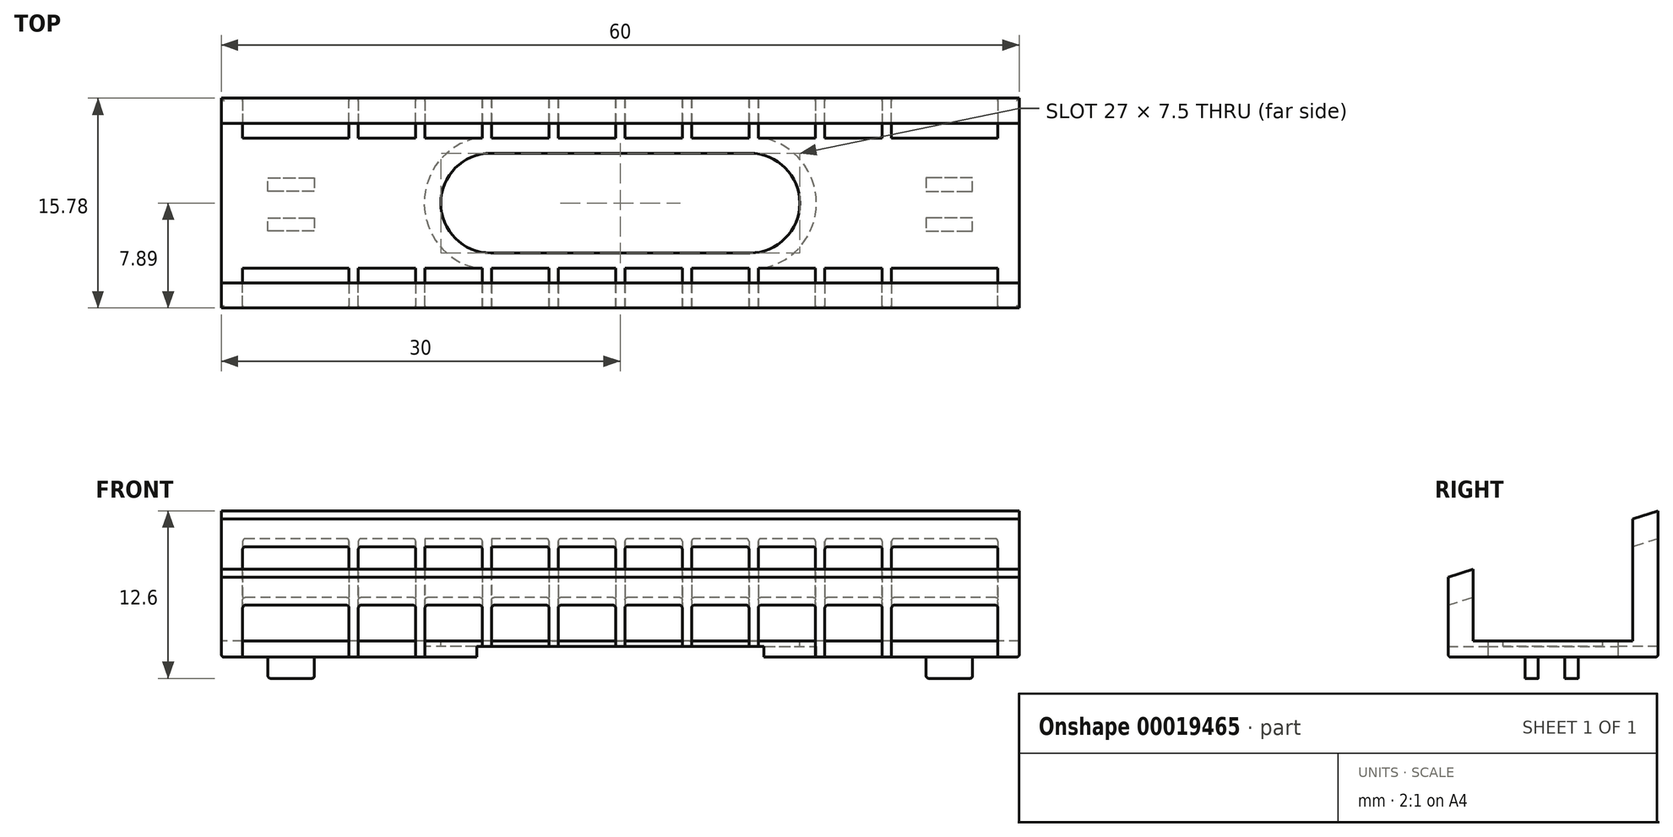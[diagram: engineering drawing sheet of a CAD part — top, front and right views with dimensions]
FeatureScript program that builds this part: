
annotation { "Feature Type Name" : "Feature", "Feature Type Description" : "" }
export const myFeature = defineFeature(function(context is Context, id is Id, definition is map)
    precondition{}
    {
        {
            var Q0;
            Q0=qCreatedBy(makeId("Top.planeOp"),FACE);
            var sketch = newSketch(context, id + "F0", { "sketchPlane" : qUnion([Q0])});
            skLineSegment(sketch, "E0.bottom", {"start": v(0, 0) * mm, "end": v(-60, 0) * mm});
            skLineSegment(sketch, "E0.top", {"start": v(0, 15.78) * mm, "end": v(-60, 15.78) * mm});
            skLineSegment(sketch, "E0.left", {"start": v(0, 0) * mm, "end": v(0, 15.78) * mm});
            skLineSegment(sketch, "E0.right", {"start": v(-60, 0) * mm, "end": v(-60, 15.78) * mm});
            skSolve(sketch);
        }
        {
            var Q0;
            Q0 = qSketchRegion(id + "F0", true);
            extrude(context, id + "F1", {"entities" : qUnion([Q0]), "depth" : 11 * mm});
        }
        {
            var Q0;
            Q0=makeQuery(id+"F1.opExtrude","SWEPT_FACE",FACE,{"disambiguationData":[OSD([sQuery(id+"F0.wireOp",EDGE,"E0.right")])]});
            var sketch = newSketch(context, id + "F2", { "sketchPlane" : qUnion([Q0])});
            skLineSegment(sketch, "E1", {"start": v(0, 6) * mm, "end": v(-1.89, 6.6) * mm});
            skLineSegment(sketch, "E2", {"start": v(-1.89, 6.6) * mm, "end": v(-1.89, 1.2) * mm});
            skLineSegment(sketch, "E3", {"start": v(-1.89, 1.2) * mm, "end": v(-13.89, 1.2) * mm});
            skLineSegment(sketch, "E4", {"start": v(-13.89, 1.2) * mm, "end": v(-13.89, 10.4) * mm});
            skLineSegment(sketch, "E5.trimOffspring", {"start": v(-13.89, 10.4) * mm, "end": v(-15.78, 11) * mm});
            skLineSegment(sketch, "E6", {"start": v(-7.89, 0) * mm, "end": v(-7.89, 1.2) * mm, "construction": true});
            skSolve(sketch);
        }
        {
            var Q0;
            {var subQ2=sQuery(id+"F2.wireOp",EDGE,"E1");Q0=makeQuery(id+"F2.imprint","IMPRINT",FACE,{"disambiguationData":[TD([[makeQuery(id+"F2.imprint","IMPRINT",EDGE,{"derivedFrom":subQ2}),-1.0]])]});}
            extrude(context, id + "F3", {"entities" : qUnion([Q0]), "operationType" : NewBodyOperationType.REMOVE, "endBound" : BoundingType.THROUGH_ALL, "oppositeDirection" : true, "depth" : 25 * mm});
        }
        {
            var Q0;
            Q0=makeQuery(id+"F3.boolean.opBoolean","COPY",FACE,{"derivedFrom":makeQuery(id+"F3.opExtrude","SWEPT_FACE",FACE,{"disambiguationData":[OSD([sQuery(id+"F2.wireOp",EDGE,"E3")])]})});
            var sketch = newSketch(context, id + "F4", { "sketchPlane" : qUnion([Q0])});
            skLineSegment(sketch, "E7", {"start": v(-30, 11.64) * mm, "end": v(-22.65, 11.64) * mm});
            skLineSegment(sketch, "E8", {"start": v(-30, 4.14) * mm, "end": v(-22.65, 4.14) * mm});
            skPoint(sketch, "E9.orphan", {"position": v(-41.1, 11.64) * mm});
            skPoint(sketch, "E10.orphan", {"position": v(-41.1, 4.14) * mm});
            skPoint(sketch, "E11.start.orphan", {"position": v(-18.9, 11.64) * mm});
            skPoint(sketch, "E12.orphan", {"position": v(-18.9, 4.14) * mm});
            skLineSegment(sketch, "E13", {"start": v(-60, 7.89) * mm, "end": v(0, 7.89) * mm, "construction": true});
            skLineSegment(sketch, "E14", {"start": v(-30, 13.89) * mm, "end": v(-30, 1.89) * mm, "construction": true});
            skLineSegment(sketch, "E15", {"start": v(-30, 7.89) * mm, "end": v(-20.25, 7.89) * mm, "construction": true});
            skArc(sketch, "E16", {"start": v(-20.25, 4.14) * mm, "mid": v(-16.5, 7.89) * mm, "end": v(-20.25, 11.64) * mm});
            skLineSegment(sketch, "E17", {"start": v(-22.65, 11.64) * mm, "end": v(-20.25, 11.64) * mm});
            skLineSegment(sketch, "E18", {"start": v(-22.65, 4.14) * mm, "end": v(-20.25, 4.14) * mm});
            skLineSegment(sketch, "E19.MirrorCS", {"start": v(-30, 4.14) * mm, "end": v(-37.35, 4.14) * mm});
            skLineSegment(sketch, "E20.MirrorCS", {"start": v(-37.35, 4.14) * mm, "end": v(-39.75, 4.14) * mm});
            skArc(sketch, "E21.MirrorCS", {"start": v(-39.75, 4.14) * mm, "mid": v(-43.5, 7.89) * mm, "end": v(-39.75, 11.64) * mm});
            skLineSegment(sketch, "E22.MirrorCS", {"start": v(-37.35, 11.64) * mm, "end": v(-39.75, 11.64) * mm});
            skLineSegment(sketch, "E23.MirrorCS", {"start": v(-30, 11.64) * mm, "end": v(-37.35, 11.64) * mm});
            skSolve(sketch);
        }
        {
            var Q0;
            Q0 = qSketchRegion(id + "F4", true);
            extrude(context, id + "F5", {"entities" : qUnion([Q0]), "operationType" : NewBodyOperationType.REMOVE, "endBound" : BoundingType.THROUGH_ALL, "oppositeDirection" : true, "depth" : 25 * mm});
        }
        {
            var Q0;
            Q0=makeQuery(id+"F1.opExtrude","CAP_FACE",FACE,{"disambiguationData":[OSD([sQuery(id+"F0.wireOp",EDGE,"E0.bottom"),sQuery(id+"F0.wireOp",EDGE,"E0.top"),sQuery(id+"F0.wireOp",EDGE,"E0.left"),sQuery(id+"F0.wireOp",EDGE,"E0.right")])],"isStart":true});
            var sketch = newSketch(context, id + "F6", { "sketchPlane" : qUnion([Q0])});
            skLineSegment(sketch, "E24", {"start": v(0, 0) * mm, "end": v(-1.6, 0) * mm});
            skLineSegment(sketch, "E25", {"start": v(-1.6, 0) * mm, "end": v(-1.6, -3) * mm});
            skLineSegment(sketch, "E26", {"start": v(-1.6, -3) * mm, "end": v(-9.6, -3) * mm});
            skLineSegment(sketch, "E27", {"start": v(-9.6, -3) * mm, "end": v(-9.6, 0) * mm});
            skLineSegment(sketch, "E28", {"start": v(-9.6, 0) * mm, "end": v(-10.3, 0) * mm});
            skLineSegment(sketch, "E29", {"start": v(-10.3, 0) * mm, "end": v(-10.3, -3) * mm});
            skLineSegment(sketch, "E30", {"start": v(-10.3, -3) * mm, "end": v(-14.61, -3) * mm});
            skLineSegment(sketch, "E31", {"start": v(-14.61, -3) * mm, "end": v(-14.61, 0) * mm});
            skLineSegment(sketch, "E32", {"start": v(-14.61, 0) * mm, "end": v(-15.31, 0) * mm});
            skLineSegment(sketch, "E33", {"start": v(-15.31, 0) * mm, "end": v(-15.31, -3) * mm});
            skLineSegment(sketch, "E34", {"start": v(-15.31, -3) * mm, "end": v(-19.62, -3) * mm});
            skLineSegment(sketch, "E35", {"start": v(-19.63, -3) * mm, "end": v(-19.63, 0) * mm});
            skLineSegment(sketch, "E36", {"start": v(-19.63, 0) * mm, "end": v(-20.33, 0) * mm});
            skLineSegment(sketch, "E37", {"start": v(-20.33, 0) * mm, "end": v(-20.33, -3) * mm});
            skLineSegment(sketch, "E38", {"start": v(-20.32, -3) * mm, "end": v(-24.64, -3) * mm});
            skLineSegment(sketch, "E39", {"start": v(-24.64, -3) * mm, "end": v(-24.64, 0) * mm});
            skLineSegment(sketch, "E40", {"start": v(-24.64, 0) * mm, "end": v(-25.34, 0) * mm});
            skLineSegment(sketch, "E41", {"start": v(-25.34, 0) * mm, "end": v(-25.34, -3) * mm});
            skLineSegment(sketch, "E42", {"start": v(-25.34, -3) * mm, "end": v(-29.65, -3) * mm});
            skLineSegment(sketch, "E43", {"start": v(-29.65, -3) * mm, "end": v(-29.65, 0) * mm});
            skLineSegment(sketch, "E44", {"start": v(-29.65, 0) * mm, "end": v(-30, 0) * mm});
            skLineSegment(sketch, "E45.MirrorCS", {"start": v(-30.35, -3) * mm, "end": v(-30.35, 0) * mm});
            skLineSegment(sketch, "E46.MirrorCS", {"start": v(-34.66, -3) * mm, "end": v(-30.35, -3) * mm});
            skLineSegment(sketch, "E47.MirrorCS", {"start": v(-34.66, 0) * mm, "end": v(-34.66, -3) * mm});
            skLineSegment(sketch, "E48.MirrorCS", {"start": v(-35.36, -3) * mm, "end": v(-35.36, 0) * mm});
            skLineSegment(sketch, "E49.MirrorCS", {"start": v(-39.68, -3) * mm, "end": v(-35.36, -3) * mm});
            skLineSegment(sketch, "E50.MirrorCS", {"start": v(-39.67, 0) * mm, "end": v(-39.67, -3) * mm});
            skLineSegment(sketch, "E51.MirrorCS", {"start": v(-40.37, -3) * mm, "end": v(-40.37, 0) * mm});
            skLineSegment(sketch, "E52.MirrorCS", {"start": v(-44.69, -3) * mm, "end": v(-40.38, -3) * mm});
            skLineSegment(sketch, "E53.MirrorCS", {"start": v(-44.69, 0) * mm, "end": v(-44.69, -3) * mm});
            skLineSegment(sketch, "E54.MirrorCS", {"start": v(-45.39, -3) * mm, "end": v(-45.39, 0) * mm});
            skLineSegment(sketch, "E55.MirrorCS", {"start": v(-49.7, -3) * mm, "end": v(-45.39, -3) * mm});
            skLineSegment(sketch, "E56.MirrorCS", {"start": v(-49.7, 0) * mm, "end": v(-49.7, -3) * mm});
            skLineSegment(sketch, "E57.MirrorCS", {"start": v(-50.4, -3) * mm, "end": v(-50.4, 0) * mm});
            skLineSegment(sketch, "E58.MirrorCS", {"start": v(-58.4, -3) * mm, "end": v(-50.4, -3) * mm});
            skLineSegment(sketch, "E59.MirrorCS", {"start": v(-58.4, 0) * mm, "end": v(-58.4, -3) * mm});
            skLineSegment(sketch, "E60.MirrorCS", {"start": v(-58.4, -15.78) * mm, "end": v(-58.4, -12.78) * mm});
            skLineSegment(sketch, "E61.MirrorCS", {"start": v(-58.4, -12.78) * mm, "end": v(-50.4, -12.78) * mm});
            skLineSegment(sketch, "E62.MirrorCS", {"start": v(-50.4, -12.78) * mm, "end": v(-50.4, -15.78) * mm});
            skLineSegment(sketch, "E63.MirrorCS", {"start": v(-49.7, -15.78) * mm, "end": v(-49.7, -12.78) * mm});
            skLineSegment(sketch, "E64.MirrorCS", {"start": v(-49.7, -12.78) * mm, "end": v(-45.39, -12.78) * mm});
            skLineSegment(sketch, "E65.MirrorCS", {"start": v(-45.39, -12.78) * mm, "end": v(-45.39, -15.78) * mm});
            skLineSegment(sketch, "E66.MirrorCS", {"start": v(-44.69, -15.78) * mm, "end": v(-44.69, -12.78) * mm});
            skLineSegment(sketch, "E67.MirrorCS", {"start": v(-44.69, -12.78) * mm, "end": v(-40.38, -12.78) * mm});
            skLineSegment(sketch, "E68.MirrorCS", {"start": v(-40.37, -12.78) * mm, "end": v(-40.37, -15.78) * mm});
            skLineSegment(sketch, "E69.MirrorCS", {"start": v(-39.67, -15.78) * mm, "end": v(-39.67, -12.78) * mm});
            skLineSegment(sketch, "E70.MirrorCS", {"start": v(-39.68, -12.78) * mm, "end": v(-35.36, -12.78) * mm});
            skLineSegment(sketch, "E71.MirrorCS", {"start": v(-35.36, -12.78) * mm, "end": v(-35.36, -15.78) * mm});
            skLineSegment(sketch, "E72.MirrorCS", {"start": v(-34.66, -12.78) * mm, "end": v(-30.35, -12.78) * mm});
            skLineSegment(sketch, "E73.MirrorCS", {"start": v(-30.35, -12.78) * mm, "end": v(-30.35, -15.78) * mm});
            skLineSegment(sketch, "E74.MirrorCS", {"start": v(-29.65, -12.78) * mm, "end": v(-29.65, -15.78) * mm});
            skLineSegment(sketch, "E75.MirrorCS", {"start": v(-25.34, -12.78) * mm, "end": v(-29.65, -12.78) * mm});
            skLineSegment(sketch, "E76.MirrorCS", {"start": v(-25.34, -15.78) * mm, "end": v(-25.34, -12.78) * mm});
            skLineSegment(sketch, "E77.MirrorCS", {"start": v(-24.64, -12.78) * mm, "end": v(-24.64, -15.78) * mm});
            skLineSegment(sketch, "E78.MirrorCS", {"start": v(-20.32, -12.78) * mm, "end": v(-24.64, -12.78) * mm});
            skLineSegment(sketch, "E79.MirrorCS", {"start": v(-20.33, -15.78) * mm, "end": v(-20.33, -12.78) * mm});
            skLineSegment(sketch, "E80.MirrorCS", {"start": v(-15.31, -12.78) * mm, "end": v(-19.62, -12.78) * mm});
            skLineSegment(sketch, "E81.MirrorCS", {"start": v(-15.31, -15.78) * mm, "end": v(-15.31, -12.78) * mm});
            skLineSegment(sketch, "E82.MirrorCS", {"start": v(-14.61, -12.78) * mm, "end": v(-14.61, -15.78) * mm});
            skLineSegment(sketch, "E83.MirrorCS", {"start": v(-10.3, -12.78) * mm, "end": v(-14.61, -12.78) * mm});
            skLineSegment(sketch, "E84.MirrorCS", {"start": v(-10.3, -15.78) * mm, "end": v(-10.3, -12.78) * mm});
            skLineSegment(sketch, "E85.MirrorCS", {"start": v(-9.6, -12.78) * mm, "end": v(-9.6, -15.78) * mm});
            skLineSegment(sketch, "E86.MirrorCS", {"start": v(-1.6, -12.78) * mm, "end": v(-9.6, -12.78) * mm});
            skLineSegment(sketch, "E87.MirrorCS", {"start": v(-1.6, -15.78) * mm, "end": v(-1.6, -12.78) * mm});
            skLineSegment(sketch, "E88", {"start": v(-19.62, -12.78) * mm, "end": v(-19.62, -15.78) * mm});
            skLineSegment(sketch, "E89", {"start": v(-34.66, -12.78) * mm, "end": v(-34.66, -15.78) * mm});
            skSolve(sketch);
        }
        {
            var Q0;
            Q0=makeQuery(id+"F3.boolean.opBoolean","COPY",FACE,{"derivedFrom":makeQuery(id+"F3.opExtrude","SWEPT_FACE",FACE,{"disambiguationData":[OSD([sQuery(id+"F2.wireOp",EDGE,"E5.trimOffspring")])]})});
            cPlane(context, id + "F7", {"entities" : qUnion([Q0]), "cplaneType" : CPlaneType.OFFSET, "offset" : 2 * mm, "oppositeDirection" : true, "width" : 150 * mm, "height" : 150 * mm});
        }
        {
            var Q0;
            Q0 = qSketchRegion(id + "F6", true);
            var Q1;
            {var subQ2=sQuery(id+"F6.wireOp",EDGE,"E60.MirrorCS");Q1=makeQuery(id+"F6.imprint","IMPRINT",FACE,{"disambiguationData":[TD([[makeQuery(id+"F6.imprint","IMPRINT",EDGE,{"derivedFrom":subQ2}),-1.0]])]});}
            var Q2;
            {var subQ2=sQuery(id+"F6.wireOp",EDGE,"E63.MirrorCS");Q2=makeQuery(id+"F6.imprint","IMPRINT",FACE,{"disambiguationData":[TD([[makeQuery(id+"F6.imprint","IMPRINT",EDGE,{"derivedFrom":subQ2}),-1.0]])]});}
            var Q3;
            {var subQ2=sQuery(id+"F6.wireOp",EDGE,"E66.MirrorCS");Q3=makeQuery(id+"F6.imprint","IMPRINT",FACE,{"disambiguationData":[TD([[makeQuery(id+"F6.imprint","IMPRINT",EDGE,{"derivedFrom":subQ2}),-1.0]])]});}
            var Q4;
            {var subQ2=sQuery(id+"F6.wireOp",EDGE,"E69.MirrorCS");Q4=makeQuery(id+"F6.imprint","IMPRINT",FACE,{"disambiguationData":[TD([[makeQuery(id+"F6.imprint","IMPRINT",EDGE,{"derivedFrom":subQ2}),-1.0]])]});}
            var Q5;
            Q5=makeQuery(id+"F6.imprint","IMPRINT",FACE,{"disambiguationData":[TD([[makeQuery(id+"F6.imprint","IMPRINT",EDGE,{"derivedFrom":sQuery(id+"F6.wireOp",EDGE,"E72.MirrorCS")}),-1.0]])]});
            var Q6;
            {var subQ2=sQuery(id+"F6.wireOp",EDGE,"E74.MirrorCS");Q6=makeQuery(id+"F6.imprint","IMPRINT",FACE,{"disambiguationData":[TD([[makeQuery(id+"F6.imprint","IMPRINT",EDGE,{"derivedFrom":subQ2}),1.0]])]});}
            var Q7;
            {var subQ2=sQuery(id+"F6.wireOp",EDGE,"E77.MirrorCS");Q7=makeQuery(id+"F6.imprint","IMPRINT",FACE,{"disambiguationData":[TD([[makeQuery(id+"F6.imprint","IMPRINT",EDGE,{"derivedFrom":subQ2}),1.0]])]});}
            var Q8;
            Q8=makeQuery(id+"F6.imprint","IMPRINT",FACE,{"disambiguationData":[TD([[makeQuery(id+"F6.imprint","IMPRINT",EDGE,{"derivedFrom":sQuery(id+"F6.wireOp",EDGE,"E80.MirrorCS")}),1.0]])]});
            var Q9;
            {var subQ2=sQuery(id+"F6.wireOp",EDGE,"E82.MirrorCS");Q9=makeQuery(id+"F6.imprint","IMPRINT",FACE,{"disambiguationData":[TD([[makeQuery(id+"F6.imprint","IMPRINT",EDGE,{"derivedFrom":subQ2}),1.0]])]});}
            var Q10;
            {var subQ2=sQuery(id+"F6.wireOp",EDGE,"E85.MirrorCS");Q10=makeQuery(id+"F6.imprint","IMPRINT",FACE,{"disambiguationData":[TD([[makeQuery(id+"F6.imprint","IMPRINT",EDGE,{"derivedFrom":subQ2}),1.0]])]});}
            var Q11;
            {var subQ2=sQuery(id+"F6.wireOp",EDGE,"E57.MirrorCS");Q11=makeQuery(id+"F6.imprint","IMPRINT",FACE,{"disambiguationData":[TD([[makeQuery(id+"F6.imprint","IMPRINT",EDGE,{"derivedFrom":subQ2}),1.0]])]});}
            var Q12;
            {var subQ2=sQuery(id+"F6.wireOp",EDGE,"E54.MirrorCS");Q12=makeQuery(id+"F6.imprint","IMPRINT",FACE,{"disambiguationData":[TD([[makeQuery(id+"F6.imprint","IMPRINT",EDGE,{"derivedFrom":subQ2}),1.0]])]});}
            var Q13;
            {var subQ2=sQuery(id+"F6.wireOp",EDGE,"E51.MirrorCS");Q13=makeQuery(id+"F6.imprint","IMPRINT",FACE,{"disambiguationData":[TD([[makeQuery(id+"F6.imprint","IMPRINT",EDGE,{"derivedFrom":subQ2}),1.0]])]});}
            var Q14;
            {var subQ2=sQuery(id+"F6.wireOp",EDGE,"E48.MirrorCS");Q14=makeQuery(id+"F6.imprint","IMPRINT",FACE,{"disambiguationData":[TD([[makeQuery(id+"F6.imprint","IMPRINT",EDGE,{"derivedFrom":subQ2}),1.0]])]});}
            var Q15;
            {var subQ2=sQuery(id+"F6.wireOp",EDGE,"E45.MirrorCS");Q15=makeQuery(id+"F6.imprint","IMPRINT",FACE,{"disambiguationData":[TD([[makeQuery(id+"F6.imprint","IMPRINT",EDGE,{"derivedFrom":subQ2}),1.0]])]});}
            var Q16;
            {var subQ2=sQuery(id+"F6.wireOp",EDGE,"E41");Q16=makeQuery(id+"F6.imprint","IMPRINT",FACE,{"disambiguationData":[TD([[makeQuery(id+"F6.imprint","IMPRINT",EDGE,{"derivedFrom":subQ2}),-1.0]])]});}
            var Q17;
            {var subQ2=sQuery(id+"F6.wireOp",EDGE,"E37");Q17=makeQuery(id+"F6.imprint","IMPRINT",FACE,{"disambiguationData":[TD([[makeQuery(id+"F6.imprint","IMPRINT",EDGE,{"derivedFrom":subQ2}),-1.0]])]});}
            var Q18;
            {var subQ2=sQuery(id+"F6.wireOp",EDGE,"E33");Q18=makeQuery(id+"F6.imprint","IMPRINT",FACE,{"disambiguationData":[TD([[makeQuery(id+"F6.imprint","IMPRINT",EDGE,{"derivedFrom":subQ2}),-1.0]])]});}
            var Q19;
            {var subQ2=sQuery(id+"F6.wireOp",EDGE,"E29");Q19=makeQuery(id+"F6.imprint","IMPRINT",FACE,{"disambiguationData":[TD([[makeQuery(id+"F6.imprint","IMPRINT",EDGE,{"derivedFrom":subQ2}),-1.0]])]});}
            var Q20;
            {var subQ2=sQuery(id+"F6.wireOp",EDGE,"E25");Q20=makeQuery(id+"F6.imprint","IMPRINT",FACE,{"disambiguationData":[TD([[makeQuery(id+"F6.imprint","IMPRINT",EDGE,{"derivedFrom":subQ2}),-1.0]])]});}
            var Q21;
            Q21=qCreatedBy(id+"F7.planeOp",FACE);
            extrude(context, id + "F8", {"entities" : qUnion([Q0, Q1, Q2, Q3, Q4, Q5, Q6, Q7, Q8, Q9, Q10, Q11, Q12, Q13, Q14, Q15, Q16, Q17, Q18, Q19, Q20]), "operationType" : NewBodyOperationType.REMOVE, "endBound" : BoundingType.UP_TO_SURFACE, "oppositeDirection" : true, "endBoundEntityFace" : qUnion([Q21]), "depth" : 25 * mm});
        }
        {
            var Q0;
            Q0=makeQuery(id+"F1.opExtrude","CAP_FACE",FACE,{"disambiguationData":[OSD([sQuery(id+"F0.wireOp",EDGE,"E0.bottom"),sQuery(id+"F0.wireOp",EDGE,"E0.top"),sQuery(id+"F0.wireOp",EDGE,"E0.left"),sQuery(id+"F0.wireOp",EDGE,"E0.right")])],"isStart":true});
            var sketch = newSketch(context, id + "F9", { "sketchPlane" : qUnion([Q0])});
            skArc(sketch, "E90", {"start": v(-19.2, -12.78) * mm, "mid": v(-15.25, -7.9) * mm, "end": v(-19.2, -3) * mm});
            skArc(sketch, "E91", {"start": v(-40.8, -3) * mm, "mid": v(-44.75, -7.9) * mm, "end": v(-40.8, -12.78) * mm});
            skLineSegment(sketch, "E92", {"start": v(-19.2, -12.78) * mm, "end": v(-19.2, -15.78) * mm});
            skLineSegment(sketch, "E93", {"start": v(-19.2, -3) * mm, "end": v(-19.2, 0) * mm});
            skLineSegment(sketch, "E94", {"start": v(-40.8, -12.78) * mm, "end": v(-40.8, -15.78) * mm});
            skLineSegment(sketch, "E95", {"start": v(-40.8, -3) * mm, "end": v(-40.8, 0) * mm});
            skLineSegment(sketch, "E96", {"start": v(-19.2, -15.78) * mm, "end": v(-40.8, -15.78) * mm});
            skLineSegment(sketch, "E97", {"start": v(-40.8, 0) * mm, "end": v(-19.2, 0) * mm});
            skSolve(sketch);
        }
        {
            var Q0;
            Q0 = qSketchRegion(id + "F9", true);
            var Q1;
            {var subQ5=sQuery(id+"F9.wireOp",EDGE,"97906bd3-8b50-4044-a8e2-cee471d0c885");Q1=makeQuery(id+"F9.imprint","IMPRINT",FACE,{"disambiguationData":[TD([[makeQuery(id+"F9.imprint","IMPRINT",EDGE,{"derivedFrom":subQ5}),1.0]])]});}
            extrude(context, id + "F10", {"entities" : qUnion([Q0, Q1]), "operationType" : NewBodyOperationType.REMOVE, "oppositeDirection" : true, "depth" : 0.8 * mm});
        }
        {
            var Q0;
            {var subQ0=sQuery(id+"F0.wireOp",EDGE,"E0.bottom");var subQ1=sQuery(id+"F0.wireOp",EDGE,"E0.top");var subQ2=sQuery(id+"F0.wireOp",EDGE,"E0.left");Q0=makeQuery(id+"F10.boolean.opBoolean","SPLIT",FACE,{"disambiguationData":[TD([makeQuery(id+"F1.opExtrude","SWEPT_FACE",FACE,{"disambiguationData":[OSD([subQ2])]})])],"derivedFrom":makeQuery(id+"F1.opExtrude","CAP_FACE",FACE,{"disambiguationData":[OSD([subQ0,subQ1,subQ2,sQuery(id+"F0.wireOp",EDGE,"E0.right")])],"isStart":true})});}
            var sketch = newSketch(context, id + "F11", { "sketchPlane" : qUnion([Q0])});
            skLineSegment(sketch, "E98", {"start": v(-7, -5.78) * mm, "end": v(-3.5, -5.78) * mm});
            skLineSegment(sketch, "E99", {"start": v(-3.5, -5.78) * mm, "end": v(-3.5, -6.78) * mm});
            skLineSegment(sketch, "E100", {"start": v(-3.5, -6.78) * mm, "end": v(-7, -6.78) * mm});
            skLineSegment(sketch, "E101", {"start": v(-7, -6.78) * mm, "end": v(-7, -5.78) * mm});
            skLineSegment(sketch, "E102", {"start": v(-7, -8.78) * mm, "end": v(-3.5, -8.78) * mm});
            skLineSegment(sketch, "E103", {"start": v(-3.5, -8.78) * mm, "end": v(-3.5, -9.78) * mm});
            skLineSegment(sketch, "E104", {"start": v(-3.5, -9.78) * mm, "end": v(-7, -9.78) * mm});
            skLineSegment(sketch, "E105", {"start": v(-7, -9.78) * mm, "end": v(-7, -8.78) * mm});
            skLineSegment(sketch, "E106.MirrorCS", {"start": v(-53, -6.78) * mm, "end": v(-53, -5.78) * mm});
            skLineSegment(sketch, "E107.MirrorCS", {"start": v(-53, -5.78) * mm, "end": v(-56.5, -5.78) * mm});
            skLineSegment(sketch, "E108.MirrorCS", {"start": v(-56.5, -5.78) * mm, "end": v(-56.5, -6.78) * mm});
            skLineSegment(sketch, "E109.MirrorCS", {"start": v(-56.5, -6.78) * mm, "end": v(-53, -6.78) * mm});
            skLineSegment(sketch, "E110.MirrorCS", {"start": v(-53, -8.78) * mm, "end": v(-56.5, -8.78) * mm});
            skLineSegment(sketch, "E111.MirrorCS", {"start": v(-56.5, -9.78) * mm, "end": v(-53, -9.78) * mm});
            skLineSegment(sketch, "E112.MirrorCS", {"start": v(-53, -9.78) * mm, "end": v(-53, -8.78) * mm});
            skLineSegment(sketch, "E113.MirrorCS", {"start": v(-56.5, -8.78) * mm, "end": v(-56.5, -9.78) * mm});
            skSolve(sketch);
        }
        {
            var Q0;
            Q0 = qSketchRegion(id + "F11", true);
            extrude(context, id + "F12", {"entities" : qUnion([Q0]), "operationType" : NewBodyOperationType.ADD, "depth" : 1.6 * mm});
        }
        {
            var Q0;
            {var subQ0=sQuery(id+"F0.wireOp",EDGE,"E0.bottom");var subQ1=sQuery(id+"F0.wireOp",EDGE,"E0.right");Q0=makeQuery(id+"F8.boolean.opBoolean","SPLIT",EDGE,{"disambiguationData":[TD([makeQuery(id+"F1.opExtrude","SWEPT_FACE",FACE,{"disambiguationData":[OSD([subQ1])]})])],"derivedFrom":makeQuery(id+"F1.opExtrude","CAP_EDGE",EDGE,{"disambiguationData":[OSD([subQ0])],"isStart":true})});}
            var Q1;
            {var subQ0=sQuery(id+"F0.wireOp",EDGE,"E0.right");var subQ1=sQuery(id+"F0.wireOp",EDGE,"E0.top");Q1=makeQuery(id+"F8.boolean.opBoolean","SPLIT",EDGE,{"disambiguationData":[TD([makeQuery(id+"F1.opExtrude","SWEPT_FACE",FACE,{"disambiguationData":[OSD([subQ0])]})])],"derivedFrom":makeQuery(id+"F1.opExtrude","CAP_EDGE",EDGE,{"disambiguationData":[OSD([subQ1])],"isStart":true})});}
            var Q2;
            {var subQ0=sQuery(id+"F0.wireOp",EDGE,"E0.left");var subQ1=sQuery(id+"F0.wireOp",EDGE,"E0.top");Q2=makeQuery(id+"F8.boolean.opBoolean","SPLIT",EDGE,{"disambiguationData":[TD([makeQuery(id+"F1.opExtrude","SWEPT_FACE",FACE,{"disambiguationData":[OSD([subQ0])]})])],"derivedFrom":makeQuery(id+"F1.opExtrude","CAP_EDGE",EDGE,{"disambiguationData":[OSD([subQ1])],"isStart":true})});}
            var Q3;
            {var subQ0=sQuery(id+"F0.wireOp",EDGE,"E0.bottom");var subQ1=sQuery(id+"F0.wireOp",EDGE,"E0.left");Q3=makeQuery(id+"F8.boolean.opBoolean","SPLIT",EDGE,{"disambiguationData":[TD([makeQuery(id+"F1.opExtrude","SWEPT_FACE",FACE,{"disambiguationData":[OSD([subQ1])]})])],"derivedFrom":makeQuery(id+"F1.opExtrude","CAP_EDGE",EDGE,{"disambiguationData":[OSD([subQ0])],"isStart":true})});}
            var Q4;
            Q4=makeQuery(id+"F1.opExtrude","CAP_EDGE",EDGE,{"disambiguationData":[OSD([sQuery(id+"F0.wireOp",EDGE,"E0.left")])],"isStart":true});
            var Q5;
            Q5=makeQuery(id+"F1.opExtrude","CAP_EDGE",EDGE,{"disambiguationData":[OSD([sQuery(id+"F0.wireOp",EDGE,"E0.right")])],"isStart":true});
            var Q6;
            Q6=makeQuery(id+"F8.boolean.opBoolean","COPY",EDGE,{"derivedFrom":makeQuery(id+"F8.opExtrude","CAP_EDGE",EDGE,{"disambiguationData":[OSD([sQuery(id+"F6.wireOp",EDGE,"E60.MirrorCS")])],"isStart":false})});
            var Q7;
            Q7=makeQuery(id+"F8.boolean.opBoolean","COPY",EDGE,{"derivedFrom":makeQuery(id+"F8.opExtrude","CAP_EDGE",EDGE,{"disambiguationData":[OSD([sQuery(id+"F6.wireOp",EDGE,"E63.MirrorCS")])],"isStart":false})});
            var Q8;
            Q8=makeQuery(id+"F8.boolean.opBoolean","COPY",EDGE,{"derivedFrom":makeQuery(id+"F8.opExtrude","CAP_EDGE",EDGE,{"disambiguationData":[OSD([sQuery(id+"F6.wireOp",EDGE,"E62.MirrorCS")])],"isStart":false})});
            var Q9;
            Q9=makeQuery(id+"F8.boolean.opBoolean","COPY",EDGE,{"derivedFrom":makeQuery(id+"F8.opExtrude","CAP_EDGE",EDGE,{"disambiguationData":[OSD([sQuery(id+"F6.wireOp",EDGE,"E65.MirrorCS")])],"isStart":false})});
            var Q10;
            Q10=makeQuery(id+"F8.boolean.opBoolean","COPY",EDGE,{"derivedFrom":makeQuery(id+"F8.opExtrude","CAP_EDGE",EDGE,{"disambiguationData":[OSD([sQuery(id+"F6.wireOp",EDGE,"E68.MirrorCS")])],"isStart":false})});
            var Q11;
            Q11=makeQuery(id+"F8.boolean.opBoolean","COPY",EDGE,{"derivedFrom":makeQuery(id+"F8.opExtrude","CAP_EDGE",EDGE,{"disambiguationData":[OSD([sQuery(id+"F6.wireOp",EDGE,"E71.MirrorCS")])],"isStart":false})});
            var Q12;
            Q12=makeQuery(id+"F8.boolean.opBoolean","COPY",EDGE,{"derivedFrom":makeQuery(id+"F8.opExtrude","CAP_EDGE",EDGE,{"disambiguationData":[OSD([sQuery(id+"F6.wireOp",EDGE,"E73.MirrorCS")])],"isStart":false})});
            var Q13;
            Q13=makeQuery(id+"F8.boolean.opBoolean","COPY",EDGE,{"derivedFrom":makeQuery(id+"F8.opExtrude","CAP_EDGE",EDGE,{"disambiguationData":[OSD([sQuery(id+"F6.wireOp",EDGE,"E76.MirrorCS")])],"isStart":false})});
            var Q14;
            Q14=makeQuery(id+"F8.boolean.opBoolean","COPY",EDGE,{"derivedFrom":makeQuery(id+"F8.opExtrude","CAP_EDGE",EDGE,{"disambiguationData":[OSD([sQuery(id+"F6.wireOp",EDGE,"E79.MirrorCS")])],"isStart":false})});
            var Q15;
            Q15=makeQuery(id+"F8.boolean.opBoolean","COPY",EDGE,{"derivedFrom":makeQuery(id+"F8.opExtrude","CAP_EDGE",EDGE,{"disambiguationData":[OSD([sQuery(id+"F6.wireOp",EDGE,"E81.MirrorCS")])],"isStart":false})});
            var Q16;
            Q16=makeQuery(id+"F8.boolean.opBoolean","COPY",EDGE,{"derivedFrom":makeQuery(id+"F8.opExtrude","CAP_EDGE",EDGE,{"disambiguationData":[OSD([sQuery(id+"F6.wireOp",EDGE,"E84.MirrorCS")])],"isStart":false})});
            var Q17;
            Q17=makeQuery(id+"F8.boolean.opBoolean","COPY",EDGE,{"derivedFrom":makeQuery(id+"F8.opExtrude","CAP_EDGE",EDGE,{"disambiguationData":[OSD([sQuery(id+"F6.wireOp",EDGE,"E87.MirrorCS")])],"isStart":false})});
            var Q18;
            Q18=makeQuery(id+"F8.boolean.opBoolean","COPY",EDGE,{"derivedFrom":makeQuery(id+"F8.opExtrude","CAP_EDGE",EDGE,{"disambiguationData":[OSD([sQuery(id+"F6.wireOp",EDGE,"E85.MirrorCS")])],"isStart":false})});
            var Q19;
            Q19=makeQuery(id+"F8.boolean.opBoolean","COPY",EDGE,{"derivedFrom":makeQuery(id+"F8.opExtrude","CAP_EDGE",EDGE,{"disambiguationData":[OSD([sQuery(id+"F6.wireOp",EDGE,"E82.MirrorCS")])],"isStart":false})});
            var Q20;
            Q20=makeQuery(id+"F8.boolean.opBoolean","COPY",EDGE,{"derivedFrom":makeQuery(id+"F8.opExtrude","CAP_EDGE",EDGE,{"disambiguationData":[OSD([sQuery(id+"F6.wireOp",EDGE,"E88")])],"isStart":false})});
            var Q21;
            Q21=makeQuery(id+"F8.boolean.opBoolean","COPY",EDGE,{"derivedFrom":makeQuery(id+"F8.opExtrude","CAP_EDGE",EDGE,{"disambiguationData":[OSD([sQuery(id+"F6.wireOp",EDGE,"E77.MirrorCS")])],"isStart":false})});
            var Q22;
            Q22=makeQuery(id+"F8.boolean.opBoolean","COPY",EDGE,{"derivedFrom":makeQuery(id+"F8.opExtrude","CAP_EDGE",EDGE,{"disambiguationData":[OSD([sQuery(id+"F6.wireOp",EDGE,"E74.MirrorCS")])],"isStart":false})});
            var Q23;
            Q23=makeQuery(id+"F8.boolean.opBoolean","COPY",EDGE,{"derivedFrom":makeQuery(id+"F8.opExtrude","CAP_EDGE",EDGE,{"disambiguationData":[OSD([sQuery(id+"F6.wireOp",EDGE,"E89")])],"isStart":false})});
            var Q24;
            {var subQ0=sQuery(id+"F0.wireOp",EDGE,"E0.top");Q24=makeQuery(id+"F8.boolean.opBoolean","SPLIT",EDGE,{"disambiguationData":[TD([makeQuery(id+"F8.opExtrude","SWEPT_FACE",FACE,{"disambiguationData":[OSD([sQuery(id+"F6.wireOp",EDGE,"E62.MirrorCS")])]})])],"derivedFrom":makeQuery(id+"F1.opExtrude","CAP_EDGE",EDGE,{"disambiguationData":[OSD([subQ0])],"isStart":true})});}
            var Q25;
            {var subQ0=sQuery(id+"F0.wireOp",EDGE,"E0.top");Q25=makeQuery(id+"F8.boolean.opBoolean","SPLIT",EDGE,{"disambiguationData":[TD([makeQuery(id+"F8.opExtrude","SWEPT_FACE",FACE,{"disambiguationData":[OSD([sQuery(id+"F6.wireOp",EDGE,"E65.MirrorCS")])]})])],"derivedFrom":makeQuery(id+"F1.opExtrude","CAP_EDGE",EDGE,{"disambiguationData":[OSD([subQ0])],"isStart":true})});}
            var Q26;
            {var subQ0=sQuery(id+"F0.wireOp",EDGE,"E0.top");Q26=makeQuery(id+"F8.boolean.opBoolean","SPLIT",EDGE,{"disambiguationData":[TD([makeQuery(id+"F8.opExtrude","SWEPT_FACE",FACE,{"disambiguationData":[OSD([sQuery(id+"F6.wireOp",EDGE,"E68.MirrorCS")])]})])],"derivedFrom":makeQuery(id+"F1.opExtrude","CAP_EDGE",EDGE,{"disambiguationData":[OSD([subQ0])],"isStart":true})});}
            var Q27;
            {var subQ0=sQuery(id+"F0.wireOp",EDGE,"E0.top");Q27=makeQuery(id+"F8.boolean.opBoolean","SPLIT",EDGE,{"disambiguationData":[TD([makeQuery(id+"F8.opExtrude","SWEPT_FACE",FACE,{"disambiguationData":[OSD([sQuery(id+"F6.wireOp",EDGE,"E71.MirrorCS")])]})])],"derivedFrom":makeQuery(id+"F1.opExtrude","CAP_EDGE",EDGE,{"disambiguationData":[OSD([subQ0])],"isStart":true})});}
            var Q28;
            {var subQ0=sQuery(id+"F0.wireOp",EDGE,"E0.top");Q28=makeQuery(id+"F8.boolean.opBoolean","SPLIT",EDGE,{"disambiguationData":[TD([makeQuery(id+"F8.opExtrude","SWEPT_FACE",FACE,{"disambiguationData":[OSD([sQuery(id+"F6.wireOp",EDGE,"E73.MirrorCS")])]})])],"derivedFrom":makeQuery(id+"F1.opExtrude","CAP_EDGE",EDGE,{"disambiguationData":[OSD([subQ0])],"isStart":true})});}
            var Q29;
            {var subQ0=sQuery(id+"F0.wireOp",EDGE,"E0.top");Q29=makeQuery(id+"F8.boolean.opBoolean","SPLIT",EDGE,{"disambiguationData":[TD([makeQuery(id+"F8.opExtrude","SWEPT_FACE",FACE,{"disambiguationData":[OSD([sQuery(id+"F6.wireOp",EDGE,"E76.MirrorCS")])]})])],"derivedFrom":makeQuery(id+"F1.opExtrude","CAP_EDGE",EDGE,{"disambiguationData":[OSD([subQ0])],"isStart":true})});}
            var Q30;
            {var subQ0=sQuery(id+"F0.wireOp",EDGE,"E0.top");Q30=makeQuery(id+"F8.boolean.opBoolean","SPLIT",EDGE,{"disambiguationData":[TD([makeQuery(id+"F8.opExtrude","SWEPT_FACE",FACE,{"disambiguationData":[OSD([sQuery(id+"F6.wireOp",EDGE,"E79.MirrorCS")])]})])],"derivedFrom":makeQuery(id+"F1.opExtrude","CAP_EDGE",EDGE,{"disambiguationData":[OSD([subQ0])],"isStart":true})});}
            var Q31;
            {var subQ0=sQuery(id+"F0.wireOp",EDGE,"E0.top");Q31=makeQuery(id+"F8.boolean.opBoolean","SPLIT",EDGE,{"disambiguationData":[TD([makeQuery(id+"F8.opExtrude","SWEPT_FACE",FACE,{"disambiguationData":[OSD([sQuery(id+"F6.wireOp",EDGE,"E81.MirrorCS")])]})])],"derivedFrom":makeQuery(id+"F1.opExtrude","CAP_EDGE",EDGE,{"disambiguationData":[OSD([subQ0])],"isStart":true})});}
            var Q32;
            {var subQ0=sQuery(id+"F0.wireOp",EDGE,"E0.top");Q32=makeQuery(id+"F8.boolean.opBoolean","SPLIT",EDGE,{"disambiguationData":[TD([makeQuery(id+"F8.opExtrude","SWEPT_FACE",FACE,{"disambiguationData":[OSD([sQuery(id+"F6.wireOp",EDGE,"E84.MirrorCS")])]})])],"derivedFrom":makeQuery(id+"F1.opExtrude","CAP_EDGE",EDGE,{"disambiguationData":[OSD([subQ0])],"isStart":true})});}
            var Q33;
            Q33=makeQuery(id+"F12.opExtrude","CAP_EDGE",EDGE,{"disambiguationData":[OSD([sQuery(id+"F11.wireOp",EDGE,"E103")])],"isStart":false});
            var Q34;
            Q34=makeQuery(id+"F12.opExtrude","CAP_EDGE",EDGE,{"disambiguationData":[OSD([sQuery(id+"F11.wireOp",EDGE,"E99")])],"isStart":false});
            var Q35;
            Q35=makeQuery(id+"F12.opExtrude","CAP_EDGE",EDGE,{"disambiguationData":[OSD([sQuery(id+"F11.wireOp",EDGE,"E101")])],"isStart":false});
            var Q36;
            Q36=makeQuery(id+"F12.opExtrude","CAP_EDGE",EDGE,{"disambiguationData":[OSD([sQuery(id+"F11.wireOp",EDGE,"E105")])],"isStart":false});
            var Q37;
            Q37=makeQuery(id+"F12.opExtrude","CAP_EDGE",EDGE,{"disambiguationData":[OSD([sQuery(id+"F11.wireOp",EDGE,"E106.MirrorCS")])],"isStart":false});
            var Q38;
            Q38=makeQuery(id+"F12.opExtrude","CAP_EDGE",EDGE,{"disambiguationData":[OSD([sQuery(id+"F11.wireOp",EDGE,"E112.MirrorCS")])],"isStart":false});
            var Q39;
            Q39=makeQuery(id+"F12.opExtrude","CAP_EDGE",EDGE,{"disambiguationData":[OSD([sQuery(id+"F11.wireOp",EDGE,"E113.MirrorCS")])],"isStart":false});
            var Q40;
            Q40=makeQuery(id+"F12.opExtrude","CAP_EDGE",EDGE,{"disambiguationData":[OSD([sQuery(id+"F11.wireOp",EDGE,"E108.MirrorCS")])],"isStart":false});
            var Q41;
            Q41=makeQuery(id+"F8.boolean.opBoolean","COPY",EDGE,{"derivedFrom":makeQuery(id+"F8.opExtrude","CAP_EDGE",EDGE,{"disambiguationData":[OSD([sQuery(id+"F6.wireOp",EDGE,"E59.MirrorCS")])],"isStart":false})});
            var Q42;
            Q42=makeQuery(id+"F8.boolean.opBoolean","COPY",EDGE,{"derivedFrom":makeQuery(id+"F8.opExtrude","CAP_EDGE",EDGE,{"disambiguationData":[OSD([sQuery(id+"F6.wireOp",EDGE,"E56.MirrorCS")])],"isStart":false})});
            var Q43;
            Q43=makeQuery(id+"F8.boolean.opBoolean","COPY",EDGE,{"derivedFrom":makeQuery(id+"F8.opExtrude","CAP_EDGE",EDGE,{"disambiguationData":[OSD([sQuery(id+"F6.wireOp",EDGE,"E53.MirrorCS")])],"isStart":false})});
            var Q44;
            Q44=makeQuery(id+"F8.boolean.opBoolean","COPY",EDGE,{"derivedFrom":makeQuery(id+"F8.opExtrude","CAP_EDGE",EDGE,{"disambiguationData":[OSD([sQuery(id+"F6.wireOp",EDGE,"E50.MirrorCS")])],"isStart":false})});
            var Q45;
            Q45=makeQuery(id+"F8.boolean.opBoolean","COPY",EDGE,{"derivedFrom":makeQuery(id+"F8.opExtrude","CAP_EDGE",EDGE,{"disambiguationData":[OSD([sQuery(id+"F6.wireOp",EDGE,"E47.MirrorCS")])],"isStart":false})});
            var Q46;
            Q46=makeQuery(id+"F8.boolean.opBoolean","COPY",EDGE,{"derivedFrom":makeQuery(id+"F8.opExtrude","CAP_EDGE",EDGE,{"disambiguationData":[OSD([sQuery(id+"F6.wireOp",EDGE,"E43")])],"isStart":false})});
            var Q47;
            Q47=makeQuery(id+"F8.boolean.opBoolean","COPY",EDGE,{"derivedFrom":makeQuery(id+"F8.opExtrude","CAP_EDGE",EDGE,{"disambiguationData":[OSD([sQuery(id+"F6.wireOp",EDGE,"E39")])],"isStart":false})});
            var Q48;
            Q48=makeQuery(id+"F8.boolean.opBoolean","COPY",EDGE,{"derivedFrom":makeQuery(id+"F8.opExtrude","CAP_EDGE",EDGE,{"disambiguationData":[OSD([sQuery(id+"F6.wireOp",EDGE,"E35")])],"isStart":false})});
            var Q49;
            Q49=makeQuery(id+"F8.boolean.opBoolean","COPY",EDGE,{"derivedFrom":makeQuery(id+"F8.opExtrude","CAP_EDGE",EDGE,{"disambiguationData":[OSD([sQuery(id+"F6.wireOp",EDGE,"E31")])],"isStart":false})});
            var Q50;
            Q50=makeQuery(id+"F8.boolean.opBoolean","COPY",EDGE,{"derivedFrom":makeQuery(id+"F8.opExtrude","CAP_EDGE",EDGE,{"disambiguationData":[OSD([sQuery(id+"F6.wireOp",EDGE,"E27")])],"isStart":false})});
            var Q51;
            {var subQ0=sQuery(id+"F0.wireOp",EDGE,"E0.bottom");Q51=makeQuery(id+"F8.boolean.opBoolean","SPLIT",EDGE,{"disambiguationData":[TD([makeQuery(id+"F8.opExtrude","SWEPT_FACE",FACE,{"disambiguationData":[OSD([sQuery(id+"F6.wireOp",EDGE,"E56.MirrorCS")])]})])],"derivedFrom":makeQuery(id+"F1.opExtrude","CAP_EDGE",EDGE,{"disambiguationData":[OSD([subQ0])],"isStart":true})});}
            var Q52;
            {var subQ0=sQuery(id+"F0.wireOp",EDGE,"E0.bottom");Q52=makeQuery(id+"F8.boolean.opBoolean","SPLIT",EDGE,{"disambiguationData":[TD([makeQuery(id+"F8.opExtrude","SWEPT_FACE",FACE,{"disambiguationData":[OSD([sQuery(id+"F6.wireOp",EDGE,"E53.MirrorCS")])]})])],"derivedFrom":makeQuery(id+"F1.opExtrude","CAP_EDGE",EDGE,{"disambiguationData":[OSD([subQ0])],"isStart":true})});}
            var Q53;
            {var subQ0=sQuery(id+"F0.wireOp",EDGE,"E0.bottom");Q53=makeQuery(id+"F8.boolean.opBoolean","SPLIT",EDGE,{"disambiguationData":[TD([makeQuery(id+"F8.opExtrude","SWEPT_FACE",FACE,{"disambiguationData":[OSD([sQuery(id+"F6.wireOp",EDGE,"E47.MirrorCS")])]})])],"derivedFrom":makeQuery(id+"F1.opExtrude","CAP_EDGE",EDGE,{"disambiguationData":[OSD([subQ0])],"isStart":true})});}
            var Q54;
            {var subQ0=sQuery(id+"F0.wireOp",EDGE,"E0.bottom");Q54=makeQuery(id+"F8.boolean.opBoolean","SPLIT",EDGE,{"disambiguationData":[TD([makeQuery(id+"F8.opExtrude","SWEPT_FACE",FACE,{"disambiguationData":[OSD([sQuery(id+"F6.wireOp",EDGE,"E50.MirrorCS")])]})])],"derivedFrom":makeQuery(id+"F1.opExtrude","CAP_EDGE",EDGE,{"disambiguationData":[OSD([subQ0])],"isStart":true})});}
            var Q55;
            {var subQ0=sQuery(id+"F0.wireOp",EDGE,"E0.bottom");Q55=makeQuery(id+"F8.boolean.opBoolean","SPLIT",EDGE,{"disambiguationData":[TD([makeQuery(id+"F8.opExtrude","SWEPT_FACE",FACE,{"disambiguationData":[OSD([sQuery(id+"F6.wireOp",EDGE,"E43")])]})])],"derivedFrom":makeQuery(id+"F1.opExtrude","CAP_EDGE",EDGE,{"disambiguationData":[OSD([subQ0])],"isStart":true})});}
            var Q56;
            {var subQ0=sQuery(id+"F0.wireOp",EDGE,"E0.bottom");Q56=makeQuery(id+"F8.boolean.opBoolean","SPLIT",EDGE,{"disambiguationData":[TD([makeQuery(id+"F8.opExtrude","SWEPT_FACE",FACE,{"disambiguationData":[OSD([sQuery(id+"F6.wireOp",EDGE,"E35")])]})])],"derivedFrom":makeQuery(id+"F1.opExtrude","CAP_EDGE",EDGE,{"disambiguationData":[OSD([subQ0])],"isStart":true})});}
            var Q57;
            {var subQ0=sQuery(id+"F0.wireOp",EDGE,"E0.bottom");Q57=makeQuery(id+"F8.boolean.opBoolean","SPLIT",EDGE,{"disambiguationData":[TD([makeQuery(id+"F8.opExtrude","SWEPT_FACE",FACE,{"disambiguationData":[OSD([sQuery(id+"F6.wireOp",EDGE,"E27")])]})])],"derivedFrom":makeQuery(id+"F1.opExtrude","CAP_EDGE",EDGE,{"disambiguationData":[OSD([subQ0])],"isStart":true})});}
            var Q58;
            {var subQ0=sQuery(id+"F0.wireOp",EDGE,"E0.bottom");Q58=makeQuery(id+"F8.boolean.opBoolean","SPLIT",EDGE,{"disambiguationData":[TD([makeQuery(id+"F8.opExtrude","SWEPT_FACE",FACE,{"disambiguationData":[OSD([sQuery(id+"F6.wireOp",EDGE,"E39")])]})])],"derivedFrom":makeQuery(id+"F1.opExtrude","CAP_EDGE",EDGE,{"disambiguationData":[OSD([subQ0])],"isStart":true})});}
            var Q59;
            {var subQ0=sQuery(id+"F0.wireOp",EDGE,"E0.bottom");Q59=makeQuery(id+"F8.boolean.opBoolean","SPLIT",EDGE,{"disambiguationData":[TD([makeQuery(id+"F8.opExtrude","SWEPT_FACE",FACE,{"disambiguationData":[OSD([sQuery(id+"F6.wireOp",EDGE,"E31")])]})])],"derivedFrom":makeQuery(id+"F1.opExtrude","CAP_EDGE",EDGE,{"disambiguationData":[OSD([subQ0])],"isStart":true})});}
            var Q60;
            Q60=makeQuery(id+"F8.boolean.opBoolean","COPY",EDGE,{"derivedFrom":makeQuery(id+"F8.opExtrude","CAP_EDGE",EDGE,{"disambiguationData":[OSD([sQuery(id+"F6.wireOp",EDGE,"E57.MirrorCS")])],"isStart":false})});
            var Q61;
            Q61=makeQuery(id+"F8.boolean.opBoolean","COPY",EDGE,{"derivedFrom":makeQuery(id+"F8.opExtrude","CAP_EDGE",EDGE,{"disambiguationData":[OSD([sQuery(id+"F6.wireOp",EDGE,"E54.MirrorCS")])],"isStart":false})});
            var Q62;
            Q62=makeQuery(id+"F8.boolean.opBoolean","COPY",EDGE,{"derivedFrom":makeQuery(id+"F8.opExtrude","CAP_EDGE",EDGE,{"disambiguationData":[OSD([sQuery(id+"F6.wireOp",EDGE,"E51.MirrorCS")])],"isStart":false})});
            var Q63;
            Q63=makeQuery(id+"F8.boolean.opBoolean","COPY",EDGE,{"derivedFrom":makeQuery(id+"F8.opExtrude","CAP_EDGE",EDGE,{"disambiguationData":[OSD([sQuery(id+"F6.wireOp",EDGE,"E48.MirrorCS")])],"isStart":false})});
            var Q64;
            Q64=makeQuery(id+"F8.boolean.opBoolean","COPY",EDGE,{"derivedFrom":makeQuery(id+"F8.opExtrude","CAP_EDGE",EDGE,{"disambiguationData":[OSD([sQuery(id+"F6.wireOp",EDGE,"E45.MirrorCS")])],"isStart":false})});
            var Q65;
            Q65=makeQuery(id+"F8.boolean.opBoolean","COPY",EDGE,{"derivedFrom":makeQuery(id+"F8.opExtrude","CAP_EDGE",EDGE,{"disambiguationData":[OSD([sQuery(id+"F6.wireOp",EDGE,"E41")])],"isStart":false})});
            var Q66;
            Q66=makeQuery(id+"F8.boolean.opBoolean","COPY",EDGE,{"derivedFrom":makeQuery(id+"F8.opExtrude","CAP_EDGE",EDGE,{"disambiguationData":[OSD([sQuery(id+"F6.wireOp",EDGE,"E37")])],"isStart":false})});
            var Q67;
            Q67=makeQuery(id+"F8.boolean.opBoolean","COPY",EDGE,{"derivedFrom":makeQuery(id+"F8.opExtrude","CAP_EDGE",EDGE,{"disambiguationData":[OSD([sQuery(id+"F6.wireOp",EDGE,"E33")])],"isStart":false})});
            var Q68;
            Q68=makeQuery(id+"F8.boolean.opBoolean","COPY",EDGE,{"derivedFrom":makeQuery(id+"F8.opExtrude","CAP_EDGE",EDGE,{"disambiguationData":[OSD([sQuery(id+"F6.wireOp",EDGE,"E29")])],"isStart":false})});
            var Q69;
            Q69=makeQuery(id+"F8.boolean.opBoolean","COPY",EDGE,{"derivedFrom":makeQuery(id+"F8.opExtrude","CAP_EDGE",EDGE,{"disambiguationData":[OSD([sQuery(id+"F6.wireOp",EDGE,"E25")])],"isStart":false})});
            fillet(context, id + "F13", {"entities" : qUnion([Q0, Q1, Q2, Q3, Q4, Q5, Q6, Q7, Q8, Q9, Q10, Q11, Q12, Q13, Q14, Q15, Q16, Q17, Q18, Q19, Q20, Q21, Q22, Q23, Q24, Q25, Q26, Q27, Q28, Q29, Q30, Q31, Q32, Q33, Q34, Q35, Q36, Q37, Q38, Q39, Q40, Q41, Q42, Q43, Q44, Q45, Q46, Q47, Q48, Q49, Q50, Q51, Q52, Q53, Q54, Q55, Q56, Q57, Q58, Q59, Q60, Q61, Q62, Q63, Q64, Q65, Q66, Q67, Q68, Q69]), "radius" : 0.2 * mm, "tangentPropagation" : true, "allowEdgeOverflow" : false});
        }
    });
